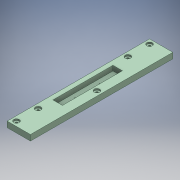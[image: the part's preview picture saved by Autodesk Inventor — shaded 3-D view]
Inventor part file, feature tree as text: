
AUTODESK INVENTOR PART (.ipt)
format: ipt  version: 2016 (Build 200138000, 138)  size: 157,696 bytes
history: native  units: mm
features: sketch x4, extrude x2, hole x2, mirror x1
ambient origin geometry x8: Origin, YZ Plane, XZ Plane, XY Plane, X Axis, Y Axis, Z Axis, Center Point
bodies: Solid1 (feature_tree)
feature tree (9):
  extrude  "baseExtrusion"  Depth=45.0mm
  hole  "xyStageAttatchM5"  [1 undecoded]
  extrude  "Extrusion2"  Depth=2.5mm
  hole  "Hole2"  [1 undecoded]
  mirror  "Mirror1"
  sketch  "Sketch1"  dims[d0=30.0mm d1=45.0mm]
  sketch  "Sketch2"  dims[d2=460.0mm d3=230.0mm]
  sketch  "Sketch3"  dims[d4=2.5mm d5=0.0mm d6=80.0mm]
  sketch  "Sketch4"  dims[d7=40.0mm d8=30.0mm d9=30.0mm d10=4.134mm d11=10.0mm d12=4.0mm d13=2.0mm d14=90.0deg d15=14.2mm d16=20.594885mm d17=194.066919mm d18=97.033459mm d19=30.783029mm d20=15.391515mm d21=16.0mm d22=0.0mm d23=15.0mm d24=70.0mm d25=6.6mm d26=6.0mm d27=18.0mm d28=4.8mm d29=90.0deg d30=8.0mm d31=20.594885mm d33=15.0mm d34=15.0mm]
note: 2 required parameter values undecoded (feature->parameter linkage not recoverable at this tier; creation-order binding heuristic only, values carry confidence <= 0.55)
